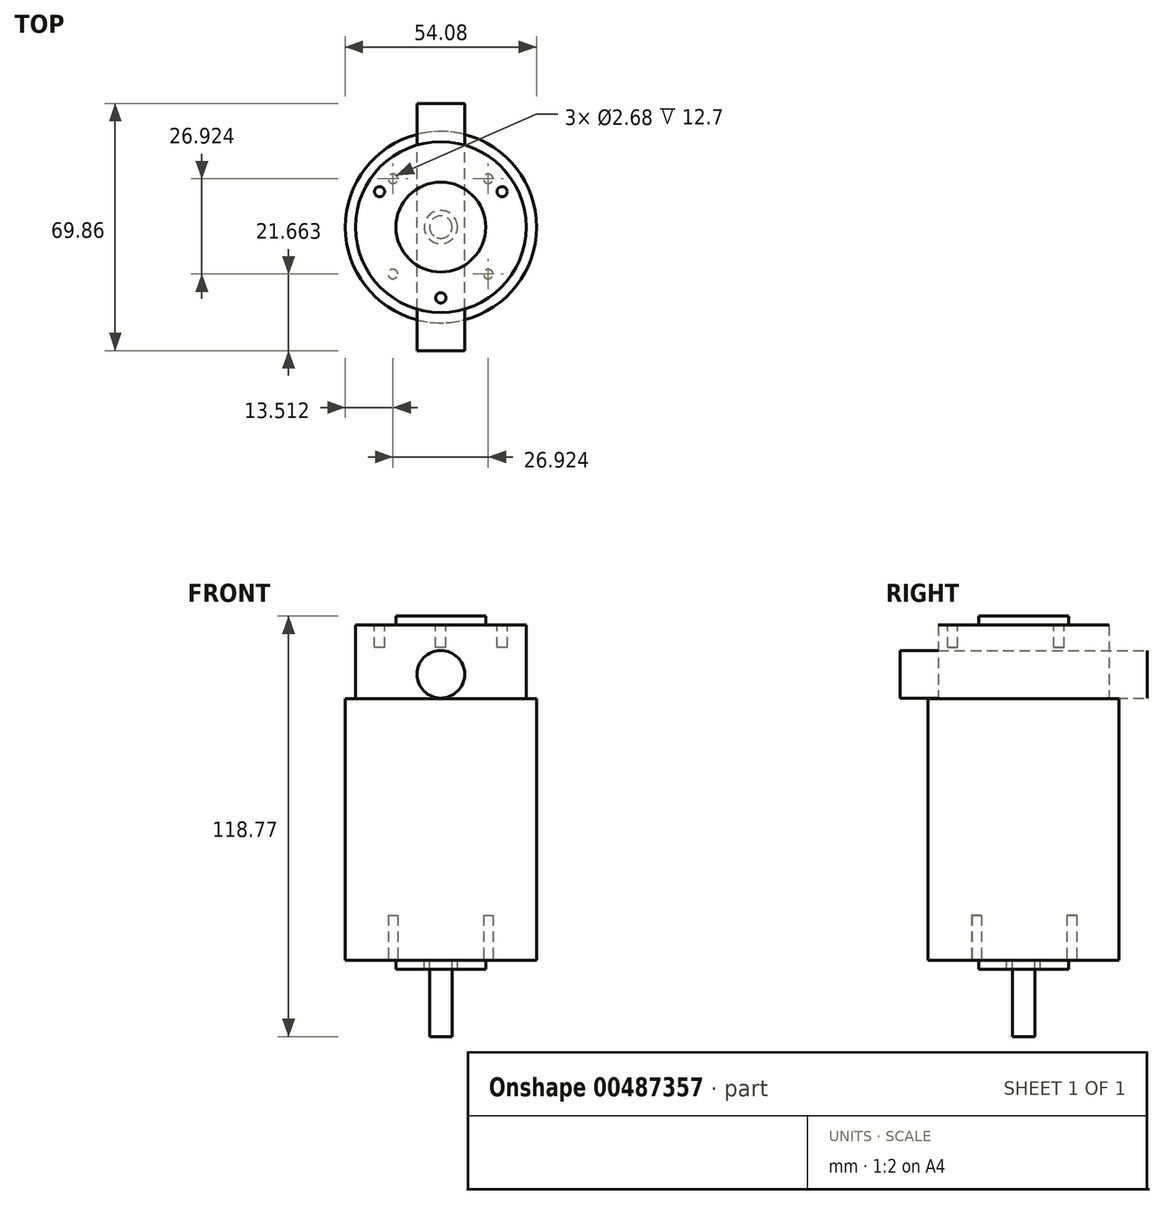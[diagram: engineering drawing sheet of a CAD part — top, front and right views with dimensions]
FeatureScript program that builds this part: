
annotation { "Feature Type Name" : "Feature", "Feature Type Description" : "" }
export const myFeature = defineFeature(function(context is Context, id is Id, definition is map)
    precondition{}
    {
        {
            var Q0;
            Q0=qCreatedBy(makeId("Top.planeOp"),FACE);
            var sketch = newSketch(context, id + "F0", { "sketchPlane" : qUnion([Q0])});
            skCircle(sketch, "E0", {"center": v(0, 0) * mm, "radius": 27.04 * mm});
            skSolve(sketch);
        }
        {
            var Q0;
            Q0=makeQuery(id+"F0.imprint","IMPRINT",FACE,{"disambiguationData":[TD([[makeQuery(id+"F0.imprint","IMPRINT",EDGE,{"derivedFrom":sQuery(id+"F0.wireOp",EDGE,"E0")}),1.0]])]});
            extrude(context, id + "F1", {"entities" : qUnion([Q0]), "depth" : 73.9 * mm});
        }
        {
            var Q0;
            Q0=makeQuery(id+"F1.opExtrude","CAP_FACE",FACE,{"disambiguationData":[OSD([sQuery(id+"F0.wireOp",EDGE,"E0")])],"isStart":false});
            var sketch = newSketch(context, id + "F2", { "sketchPlane" : qUnion([Q0])});
            skCircle(sketch, "E1", {"center": v(0, 0) * mm, "radius": 24.13 * mm});
            skSolve(sketch);
        }
        {
            var Q0;
            Q0=makeQuery(id+"F2.imprint","IMPRINT",FACE,{"disambiguationData":[TD([[makeQuery(id+"F2.imprint","IMPRINT",EDGE,{"derivedFrom":sQuery(id+"F2.wireOp",EDGE,"E1")}),1.0]])]});
            extrude(context, id + "F3", {"entities" : qUnion([Q0]), "operationType" : NewBodyOperationType.ADD, "depth" : 20.73 * mm, "offsetDistance" : 25.4 * mm});
        }
        {
            var Q0;
            Q0=makeQuery(id+"F3.opExtrude","CAP_FACE",FACE,{"disambiguationData":[OSD([sQuery(id+"F2.wireOp",EDGE,"E1")])],"isStart":false});
            var sketch = newSketch(context, id + "F4", { "sketchPlane" : qUnion([Q0])});
            skCircle(sketch, "E2", {"center": v(0, 0) * mm, "radius": 12.7 * mm});
            skSolve(sketch);
        }
        {
            var Q0;
            Q0=makeQuery(id+"F4.imprint","IMPRINT",FACE,{"disambiguationData":[TD([[makeQuery(id+"F4.imprint","IMPRINT",EDGE,{"derivedFrom":sQuery(id+"F4.wireOp",EDGE,"E2")}),1.0]])]});
            extrude(context, id + "F5", {"entities" : qUnion([Q0]), "operationType" : NewBodyOperationType.ADD, "depth" : 2.54 * mm, "offsetDistance" : 25.4 * mm});
        }
        {
            var Q0;
            Q0=makeQuery(id+"F1.opExtrude","CAP_FACE",FACE,{"disambiguationData":[OSD([sQuery(id+"F0.wireOp",EDGE,"E0")])],"isStart":true});
            var sketch = newSketch(context, id + "F6", { "sketchPlane" : qUnion([Q0])});
            skCircle(sketch, "E3", {"center": v(0, 0) * mm, "radius": 12.7 * mm});
            skCircle(sketch, "E4", {"center": v(0, 0) * mm, "radius": 4.7 * mm});
            skSolve(sketch);
        }
        {
            var Q0;
            Q0=makeQuery(id+"F6.imprint","IMPRINT",FACE,{"disambiguationData":[TD([[makeQuery(id+"F6.imprint","IMPRINT",EDGE,{"derivedFrom":sQuery(id+"F6.wireOp",EDGE,"E3")}),1.0]])]});
            extrude(context, id + "F7", {"entities" : qUnion([Q0]), "operationType" : NewBodyOperationType.ADD, "depth" : 2.54 * mm});
        }
        {
            var Q0;
            Q0=makeQuery(id+"F7.boolean.opBoolean","SPLIT",FACE,{"disambiguationData":[TD([makeQuery(id+"F7.opExtrude","SWEPT_FACE",FACE,{"disambiguationData":[OSD([sQuery(id+"F6.wireOp",EDGE,"E4")])]})])],"derivedFrom":makeQuery(id+"F1.opExtrude","CAP_FACE",FACE,{"disambiguationData":[OSD([sQuery(id+"F0.wireOp",EDGE,"E0")])],"isStart":true})});
            var sketch = newSketch(context, id + "F8", { "sketchPlane" : qUnion([Q0])});
            skCircle(sketch, "E5", {"center": v(0, 0) * mm, "radius": 3.18 * mm});
            skSolve(sketch);
        }
        {
            var Q0;
            Q0=makeQuery(id+"F8.imprint","IMPRINT",FACE,{"disambiguationData":[TD([[makeQuery(id+"F8.imprint","IMPRINT",EDGE,{"derivedFrom":sQuery(id+"F8.wireOp",EDGE,"E5")}),1.0]])]});
            extrude(context, id + "F9", {"entities" : qUnion([Q0]), "operationType" : NewBodyOperationType.ADD, "depth" : 21.59 * mm});
        }
        {
            var Q0;
            Q0=qCreatedBy(makeId("Front.planeOp"),FACE);
            var sketch = newSketch(context, id + "F10", { "sketchPlane" : qUnion([Q0])});
            skCircle(sketch, "E6", {"center": v(0, 80.77) * mm, "radius": 6.73 * mm});
            skSolve(sketch);
        }
        {
            var Q0;
            Q0=makeQuery(id+"F10.imprint","IMPRINT",FACE,{"disambiguationData":[TD([[makeQuery(id+"F10.imprint","IMPRINT",EDGE,{"derivedFrom":sQuery(id+"F10.wireOp",EDGE,"E6")}),1.0]])]});
            var Q1;
            Q1=sQuery(id+"F10.wireOp",EDGE,"E6");
            extrude(context, id + "F11", {"entities" : qUnion([Q0]), "surfaceEntities" : qUnion([Q1]), "depth" : 69.85 * mm, "symmetric" : true});
        }
        {
            var Q0;
            Q0=makeQuery(id+"F3.opExtrude","CAP_FACE",FACE,{"disambiguationData":[OSD([sQuery(id+"F2.wireOp",EDGE,"E1")])],"isStart":false});
            var sketch = newSketch(context, id + "F12", { "sketchPlane" : qUnion([Q0])});
            skLineSegment(sketch, "E7", {"start": v(0, 24.13) * mm, "end": v(0, -24.13) * mm});
            skLineSegment(sketch, "E8", {"start": v(0, 0) * mm, "end": v(20.9, 12.07) * mm});
            skLineSegment(sketch, "E9", {"start": v(0, 0) * mm, "end": v(-20.9, 12.07) * mm});
            skCircle(sketch, "E10", {"center": v(17.32, 10) * mm, "radius": 1.45 * mm});
            skCircle(sketch, "E11", {"center": v(-17.32, 10) * mm, "radius": 1.45 * mm});
            skCircle(sketch, "E12", {"center": v(0, -20) * mm, "radius": 1.45 * mm});
            skSolve(sketch);
        }
        {
            var Q0;
            {var subQ0=sQuery(id+"F12.wireOp",EDGE,"E11");var subQ1=sQuery(id+"F12.wireOp",EDGE,"E9");var subQ2=makeQuery(id+"F12.imprint","INTERSECT",VERTEX,{"disambiguationData":[OD(0.0)],"derivedFrom":[subQ1,subQ0]});Q0=makeQuery(id+"F12.imprint","IMPRINT",FACE,{"disambiguationData":[TD([[makeQuery(id+"F12.imprint","IMPRINT",EDGE,{"disambiguationData":[TD([[subQ2,-1.0]])],"derivedFrom":subQ1}),-1.0]])]});}
            var Q1;
            {var subQ0=sQuery(id+"F12.wireOp",EDGE,"E11");var subQ1=sQuery(id+"F12.wireOp",EDGE,"E9");var subQ2=makeQuery(id+"F12.imprint","INTERSECT",VERTEX,{"disambiguationData":[OD(0.0)],"derivedFrom":[subQ1,subQ0]});Q1=makeQuery(id+"F12.imprint","IMPRINT",FACE,{"disambiguationData":[TD([[makeQuery(id+"F12.imprint","IMPRINT",EDGE,{"disambiguationData":[TD([[subQ2,-1.0]])],"derivedFrom":subQ1}),1.0]])]});}
            var Q2;
            {var subQ0=sQuery(id+"F12.wireOp",EDGE,"E12");var subQ1=sQuery(id+"F12.wireOp",EDGE,"E7");var subQ2=makeQuery(id+"F12.imprint","INTERSECT",VERTEX,{"disambiguationData":[OD(0.0)],"derivedFrom":[subQ1,subQ0]});Q2=makeQuery(id+"F12.imprint","IMPRINT",FACE,{"disambiguationData":[TD([[makeQuery(id+"F12.imprint","IMPRINT",EDGE,{"disambiguationData":[TD([[subQ2,-1.0]])],"derivedFrom":subQ1}),1.0]])]});}
            var Q3;
            {var subQ0=sQuery(id+"F12.wireOp",EDGE,"E12");var subQ1=sQuery(id+"F12.wireOp",EDGE,"E7");var subQ2=makeQuery(id+"F12.imprint","INTERSECT",VERTEX,{"disambiguationData":[OD(0.0)],"derivedFrom":[subQ1,subQ0]});Q3=makeQuery(id+"F12.imprint","IMPRINT",FACE,{"disambiguationData":[TD([[makeQuery(id+"F12.imprint","IMPRINT",EDGE,{"disambiguationData":[TD([[subQ2,-1.0]])],"derivedFrom":subQ1}),-1.0]])]});}
            var Q4;
            {var subQ0=sQuery(id+"F12.wireOp",EDGE,"E10");var subQ1=sQuery(id+"F12.wireOp",EDGE,"E8");var subQ2=makeQuery(id+"F12.imprint","INTERSECT",VERTEX,{"disambiguationData":[OD(0.0)],"derivedFrom":[subQ1,subQ0]});Q4=makeQuery(id+"F12.imprint","IMPRINT",FACE,{"disambiguationData":[TD([[makeQuery(id+"F12.imprint","IMPRINT",EDGE,{"disambiguationData":[TD([[subQ2,-1.0]])],"derivedFrom":subQ1}),1.0]])]});}
            var Q5;
            {var subQ0=sQuery(id+"F12.wireOp",EDGE,"E10");var subQ1=sQuery(id+"F12.wireOp",EDGE,"E8");var subQ2=makeQuery(id+"F12.imprint","INTERSECT",VERTEX,{"disambiguationData":[OD(0.0)],"derivedFrom":[subQ1,subQ0]});Q5=makeQuery(id+"F12.imprint","IMPRINT",FACE,{"disambiguationData":[TD([[makeQuery(id+"F12.imprint","IMPRINT",EDGE,{"disambiguationData":[TD([[subQ2,-1.0]])],"derivedFrom":subQ1}),-1.0]])]});}
            extrude(context, id + "F13", {"entities" : qUnion([Q0, Q1, Q2, Q3, Q4, Q5]), "operationType" : NewBodyOperationType.REMOVE, "oppositeDirection" : true, "depth" : 6.35 * mm, "offsetDistance" : 25.4 * mm});
        }
        {
            var Q0;
            Q0=makeQuery(id+"F6.imprint","IMPRINT",FACE,{"disambiguationData":[TD([[makeQuery(id+"F6.imprint","IMPRINT",EDGE,{"derivedFrom":sQuery(id+"F6.wireOp",EDGE,"E3")}),-1.0]])]});
            var sketch = newSketch(context, id + "F14", { "sketchPlane" : qUnion([Q0])});
            skLineSegment(sketch, "E13.bottom", {"start": v(-13.53, 13.27) * mm, "end": v(13.4, 13.27) * mm});
            skLineSegment(sketch, "E13.top", {"start": v(-13.53, -13.66) * mm, "end": v(13.4, -13.66) * mm});
            skLineSegment(sketch, "E13.left", {"start": v(-13.53, 13.27) * mm, "end": v(-13.53, -13.66) * mm});
            skLineSegment(sketch, "E13.right", {"start": v(13.4, 13.27) * mm, "end": v(13.4, -13.66) * mm});
            skCircle(sketch, "E14", {"center": v(13.4, 13.27) * mm, "radius": 1.34 * mm});
            skCircle(sketch, "E15", {"center": v(-13.53, 13.27) * mm, "radius": 1.35 * mm});
            skCircle(sketch, "E16", {"center": v(-13.53, -13.66) * mm, "radius": 1.34 * mm});
            skCircle(sketch, "E17", {"center": v(13.4, -13.66) * mm, "radius": 1.34 * mm});
            skSolve(sketch);
        }
        {
            var Q0;
            {var subQ0=sQuery(id+"F14.wireOp",EDGE,"E13.right");var subQ1=sQuery(id+"F14.wireOp",EDGE,"E13.bottom");var subQ2=makeQuery(id+"F14.imprint","INTERSECT",VERTEX,{"derivedFrom":[subQ1,subQ0]});Q0=makeQuery(id+"F14.imprint","IMPRINT",FACE,{"disambiguationData":[TD([[makeQuery(id+"F14.imprint","IMPRINT",EDGE,{"disambiguationData":[TD([[subQ2,1.0]])],"derivedFrom":subQ1}),1.0]])]});}
            var Q1;
            {var subQ0=sQuery(id+"F14.wireOp",EDGE,"E13.right");var subQ1=sQuery(id+"F14.wireOp",EDGE,"E13.bottom");var subQ2=makeQuery(id+"F14.imprint","INTERSECT",VERTEX,{"derivedFrom":[subQ1,subQ0]});Q1=makeQuery(id+"F14.imprint","IMPRINT",FACE,{"disambiguationData":[TD([[makeQuery(id+"F14.imprint","IMPRINT",EDGE,{"disambiguationData":[TD([[subQ2,1.0]])],"derivedFrom":subQ1}),-1.0]])]});}
            var Q2;
            {var subQ0=sQuery(id+"F14.wireOp",EDGE,"E13.right");var subQ1=sQuery(id+"F14.wireOp",EDGE,"E13.top");var subQ2=makeQuery(id+"F14.imprint","INTERSECT",VERTEX,{"derivedFrom":[subQ1,subQ0]});Q2=makeQuery(id+"F14.imprint","IMPRINT",FACE,{"disambiguationData":[TD([[makeQuery(id+"F14.imprint","IMPRINT",EDGE,{"disambiguationData":[TD([[subQ2,1.0]])],"derivedFrom":subQ1}),-1.0]])]});}
            var Q3;
            {var subQ0=sQuery(id+"F14.wireOp",EDGE,"E13.right");var subQ1=sQuery(id+"F14.wireOp",EDGE,"E13.top");var subQ2=makeQuery(id+"F14.imprint","INTERSECT",VERTEX,{"derivedFrom":[subQ1,subQ0]});Q3=makeQuery(id+"F14.imprint","IMPRINT",FACE,{"disambiguationData":[TD([[makeQuery(id+"F14.imprint","IMPRINT",EDGE,{"disambiguationData":[TD([[subQ2,1.0]])],"derivedFrom":subQ1}),1.0]])]});}
            var Q4;
            {var subQ0=sQuery(id+"F14.wireOp",EDGE,"E13.left");var subQ1=sQuery(id+"F14.wireOp",EDGE,"E13.bottom");var subQ2=makeQuery(id+"F14.imprint","INTERSECT",VERTEX,{"derivedFrom":[subQ1,subQ0]});Q4=makeQuery(id+"F14.imprint","IMPRINT",FACE,{"disambiguationData":[TD([[makeQuery(id+"F14.imprint","IMPRINT",EDGE,{"disambiguationData":[TD([[subQ2,-1.0]])],"derivedFrom":subQ1}),-1.0]])]});}
            var Q5;
            {var subQ0=sQuery(id+"F14.wireOp",EDGE,"E13.left");var subQ1=sQuery(id+"F14.wireOp",EDGE,"E13.bottom");var subQ2=makeQuery(id+"F14.imprint","INTERSECT",VERTEX,{"derivedFrom":[subQ1,subQ0]});Q5=makeQuery(id+"F14.imprint","IMPRINT",FACE,{"disambiguationData":[TD([[makeQuery(id+"F14.imprint","IMPRINT",EDGE,{"disambiguationData":[TD([[subQ2,-1.0]])],"derivedFrom":subQ1}),1.0]])]});}
            var Q6;
            {var subQ0=sQuery(id+"F14.wireOp",EDGE,"E13.left");var subQ1=sQuery(id+"F14.wireOp",EDGE,"E13.top");var subQ2=makeQuery(id+"F14.imprint","INTERSECT",VERTEX,{"derivedFrom":[subQ1,subQ0]});Q6=makeQuery(id+"F14.imprint","IMPRINT",FACE,{"disambiguationData":[TD([[makeQuery(id+"F14.imprint","IMPRINT",EDGE,{"disambiguationData":[TD([[subQ2,-1.0]])],"derivedFrom":subQ1}),1.0]])]});}
            var Q7;
            {var subQ0=sQuery(id+"F14.wireOp",EDGE,"E13.left");var subQ1=sQuery(id+"F14.wireOp",EDGE,"E13.top");var subQ2=makeQuery(id+"F14.imprint","INTERSECT",VERTEX,{"derivedFrom":[subQ1,subQ0]});Q7=makeQuery(id+"F14.imprint","IMPRINT",FACE,{"disambiguationData":[TD([[makeQuery(id+"F14.imprint","IMPRINT",EDGE,{"disambiguationData":[TD([[subQ2,-1.0]])],"derivedFrom":subQ1}),-1.0]])]});}
            extrude(context, id + "F15", {"entities" : qUnion([Q0, Q1, Q2, Q3, Q4, Q5, Q6, Q7]), "operationType" : NewBodyOperationType.REMOVE, "oppositeDirection" : true, "depth" : 12.7 * mm, "offsetDistance" : 25.4 * mm});
        }
    });
